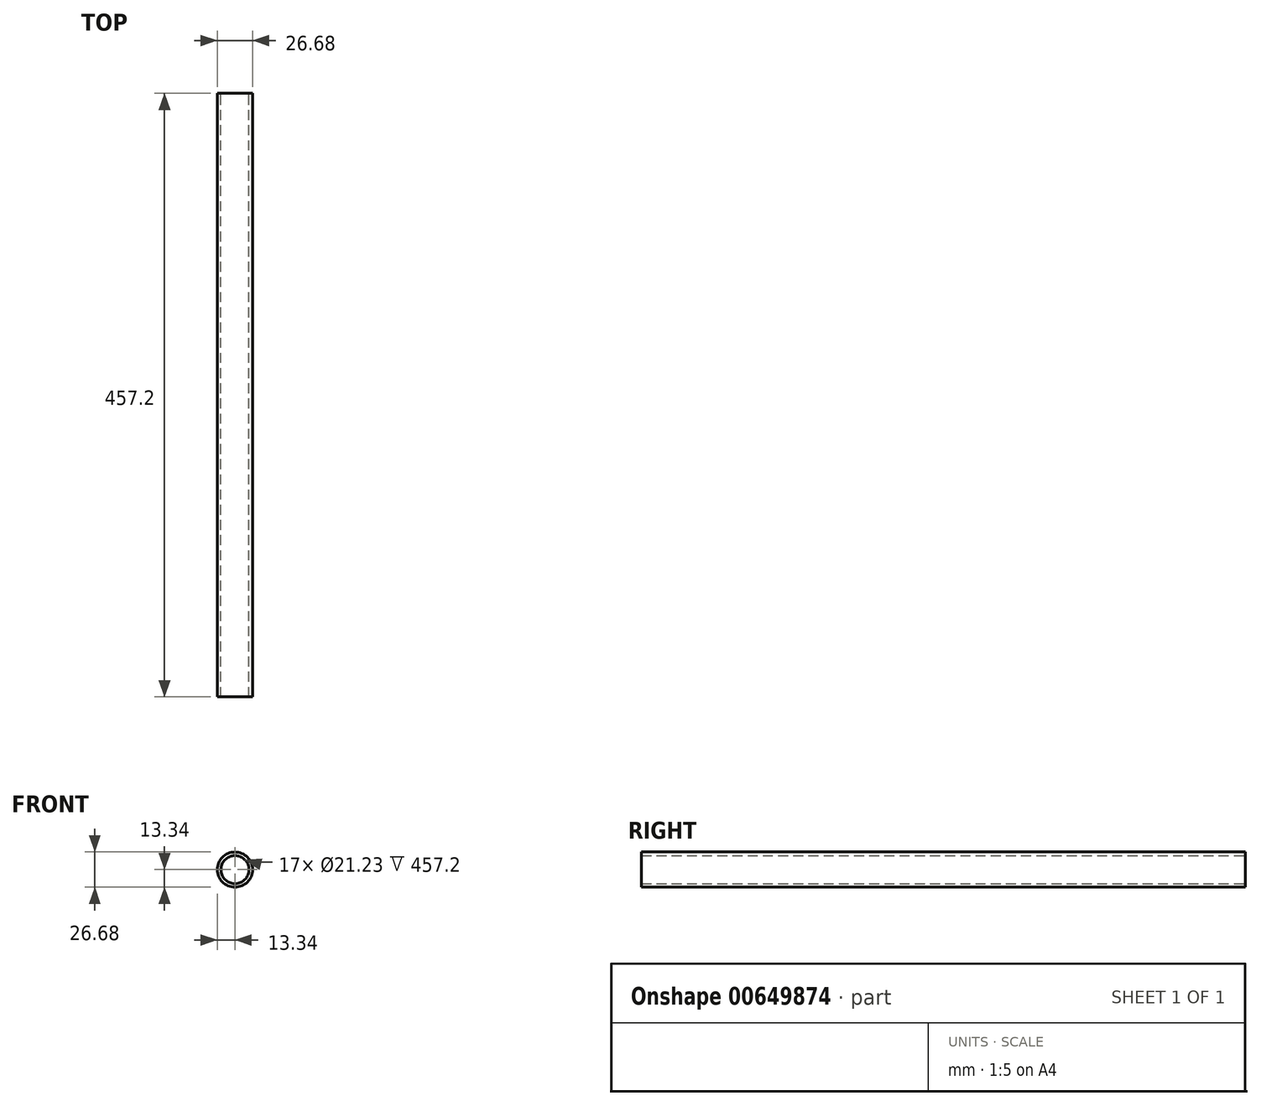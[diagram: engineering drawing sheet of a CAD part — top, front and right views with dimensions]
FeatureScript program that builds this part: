
annotation { "Feature Type Name" : "Feature", "Feature Type Description" : "" }
export const myFeature = defineFeature(function(context is Context, id is Id, definition is map)
    precondition{}
    {
        {
            var Q0;
            Q0=qCreatedBy(makeId("Front.planeOp"),FACE);
            var sketch = newSketch(context, id + "F0", { "sketchPlane" : qUnion([Q0])});
            skCircle(sketch, "E0", {"center": v(0, 0) * mm, "radius": 13.34 * mm});
            skCircle(sketch, "E1", {"center": v(0, 0) * mm, "radius": 10.62 * mm});
            skSolve(sketch);
        }
        {
            var Q0;
            Q0 = qSketchRegion(id + "F0", true);
            extrude(context, id + "F1", {"entities" : qUnion([Q0]), "depth" : 457.2 * mm, "offsetDistance" : 25.4 * mm});
        }
    });
